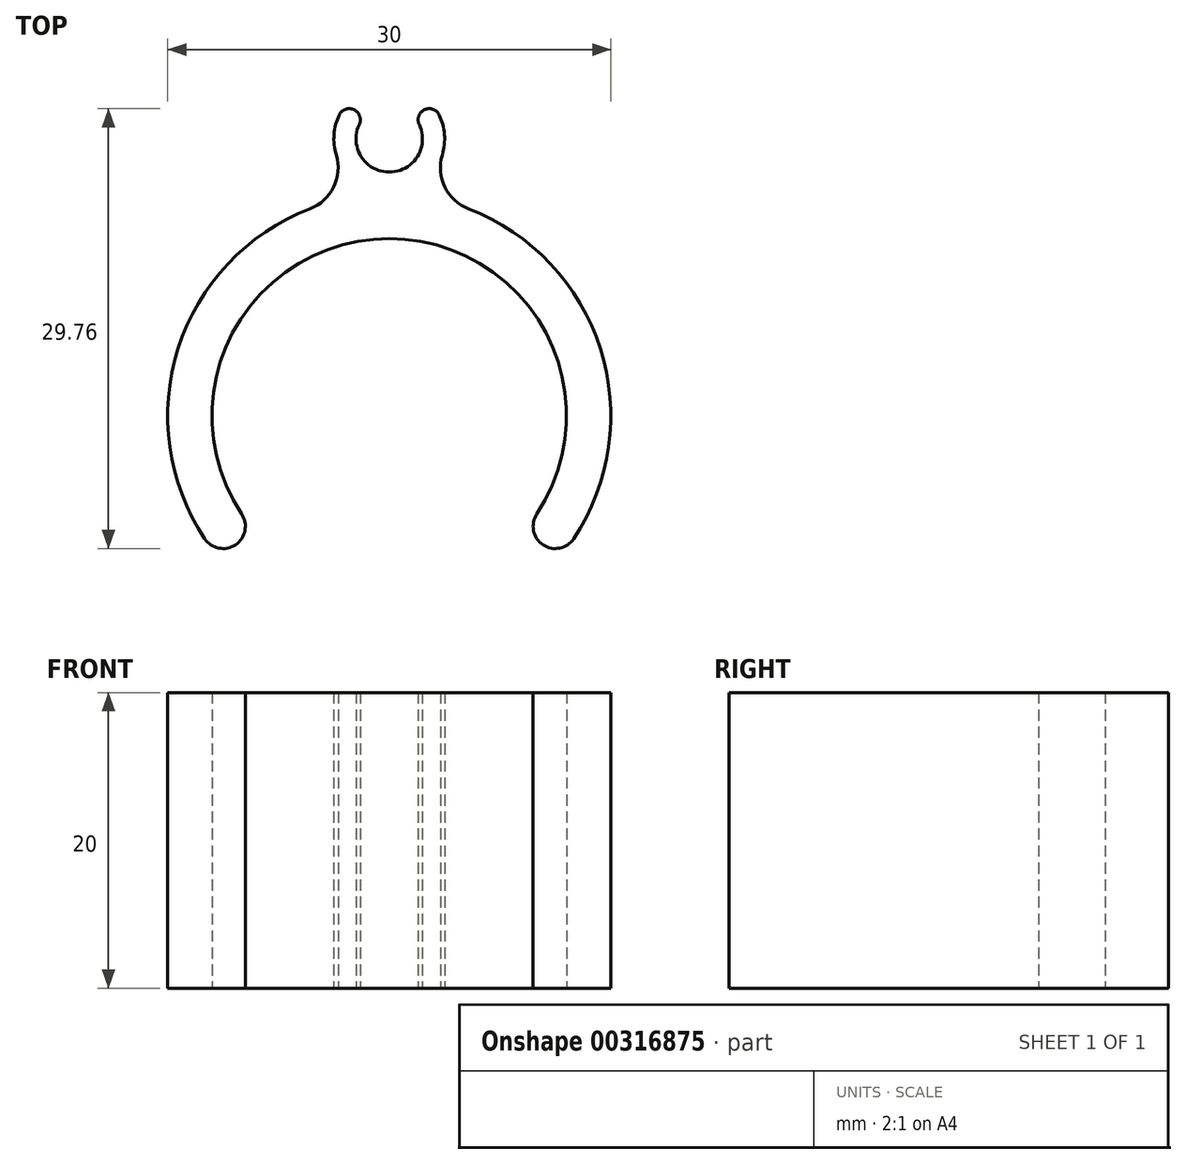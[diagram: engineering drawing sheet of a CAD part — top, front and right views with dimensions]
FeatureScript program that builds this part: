
annotation { "Feature Type Name" : "Feature", "Feature Type Description" : "" }
export const myFeature = defineFeature(function(context is Context, id is Id, definition is map)
    precondition{}
    {
        {
            var Q0;
            Q0=qCreatedBy(makeId("Top.planeOp"),FACE);
            var sketch = newSketch(context, id + "F0", { "sketchPlane" : qUnion([Q0])});
            skArc(sketch, "E0", {"start": v(10, -6.64) * mm, "mid": v(0, 12) * mm, "end": v(-10, -6.64) * mm});
            skArc(sketch, "E1", {"start": v(-5.39, 14) * mm, "mid": v(-14.3, 4.55) * mm, "end": v(-12.5, -8.3) * mm});
            skArc(sketch, "E2", {"start": v(-2.03, 19.72) * mm, "mid": v(0, 16.5) * mm, "end": v(2.03, 19.72) * mm});
            skArc(sketch, "E3", {"start": v(-3.38, 20.37) * mm, "mid": v(-3.74, 19.04) * mm, "end": v(-3.6, 17.67) * mm});
            skLineSegment(sketch, "E4", {"start": v(-10.28, -8.62) * mm, "end": v(-10.28, -8.62) * mm});
            skLineSegment(sketch, "E5", {"start": v(10.28, -8.62) * mm, "end": v(10.28, -8.62) * mm});
            skLineSegment(sketch, "E6", {"start": v(-2.23, 20.62) * mm, "end": v(-2.23, 20.62) * mm});
            skLineSegment(sketch, "E7", {"start": v(2.23, 20.62) * mm, "end": v(2.23, 20.62) * mm});
            skArc(sketch, "E8.filletArc", {"start": v(-5.39, 14) * mm, "mid": v(-3.77, 15.48) * mm, "end": v(-3.6, 17.67) * mm});
            skArc(sketch, "E9.MirrorCS", {"start": v(3.38, 20.37) * mm, "mid": v(3.74, 19.04) * mm, "end": v(3.6, 17.67) * mm});
            skArc(sketch, "E10.MirrorCS", {"start": v(5.39, 14) * mm, "mid": v(3.77, 15.48) * mm, "end": v(3.6, 17.67) * mm});
            skArc(sketch, "E11.MirrorCS", {"start": v(5.39, 14) * mm, "mid": v(14.3, 4.55) * mm, "end": v(12.5, -8.3) * mm});
            skPoint(sketch, "E12.visualSharp", {"position": v(-11.5, -9.64) * mm});
            skArc(sketch, "E12.filletArc", {"start": v(-12.5, -8.3) * mm, "mid": v(-11.46, -8.96) * mm, "end": v(-10.28, -8.62) * mm});
            skPoint(sketch, "E13.visualSharp", {"position": v(-9.2, -7.71) * mm});
            skArc(sketch, "E13.filletArc", {"start": v(-10.28, -8.62) * mm, "mid": v(-9.76, -7.69) * mm, "end": v(-10, -6.64) * mm});
            skPoint(sketch, "E14.visualSharp", {"position": v(9.2, -7.71) * mm});
            skArc(sketch, "E14.filletArc", {"start": v(10, -6.64) * mm, "mid": v(9.76, -7.69) * mm, "end": v(10.28, -8.62) * mm});
            skPoint(sketch, "E15.newPointB", {"position": v(11.5, -9.64) * mm});
            skArc(sketch, "E15.filletArc", {"start": v(10.28, -8.62) * mm, "mid": v(11.46, -8.96) * mm, "end": v(12.5, -8.3) * mm});
            skPoint(sketch, "E16.visualSharp", {"position": v(-2.87, 21.16) * mm});
            skArc(sketch, "E16.filletArc", {"start": v(-2.23, 20.62) * mm, "mid": v(-2.87, 20.78) * mm, "end": v(-3.38, 20.37) * mm});
            skPoint(sketch, "E17.visualSharp", {"position": v(-1.72, 20.2) * mm});
            skArc(sketch, "E17.filletArc", {"start": v(-2.03, 19.72) * mm, "mid": v(-1.97, 20.2) * mm, "end": v(-2.23, 20.62) * mm});
            skPoint(sketch, "E18.visualSharp", {"position": v(1.72, 20.2) * mm});
            skArc(sketch, "E18.filletArc", {"start": v(2.23, 20.62) * mm, "mid": v(1.97, 20.2) * mm, "end": v(2.03, 19.72) * mm});
            skPoint(sketch, "E19.visualSharp", {"position": v(2.87, 21.16) * mm});
            skArc(sketch, "E19.filletArc", {"start": v(3.38, 20.37) * mm, "mid": v(2.87, 20.78) * mm, "end": v(2.23, 20.62) * mm});
            skSolve(sketch);
        }
        {
            var Q0;
            Q0 = qSketchRegion(id + "F0", true);
            extrude(context, id + "F1", {"entities" : qUnion([Q0]), "depth" : 20 * mm});
        }
    });
